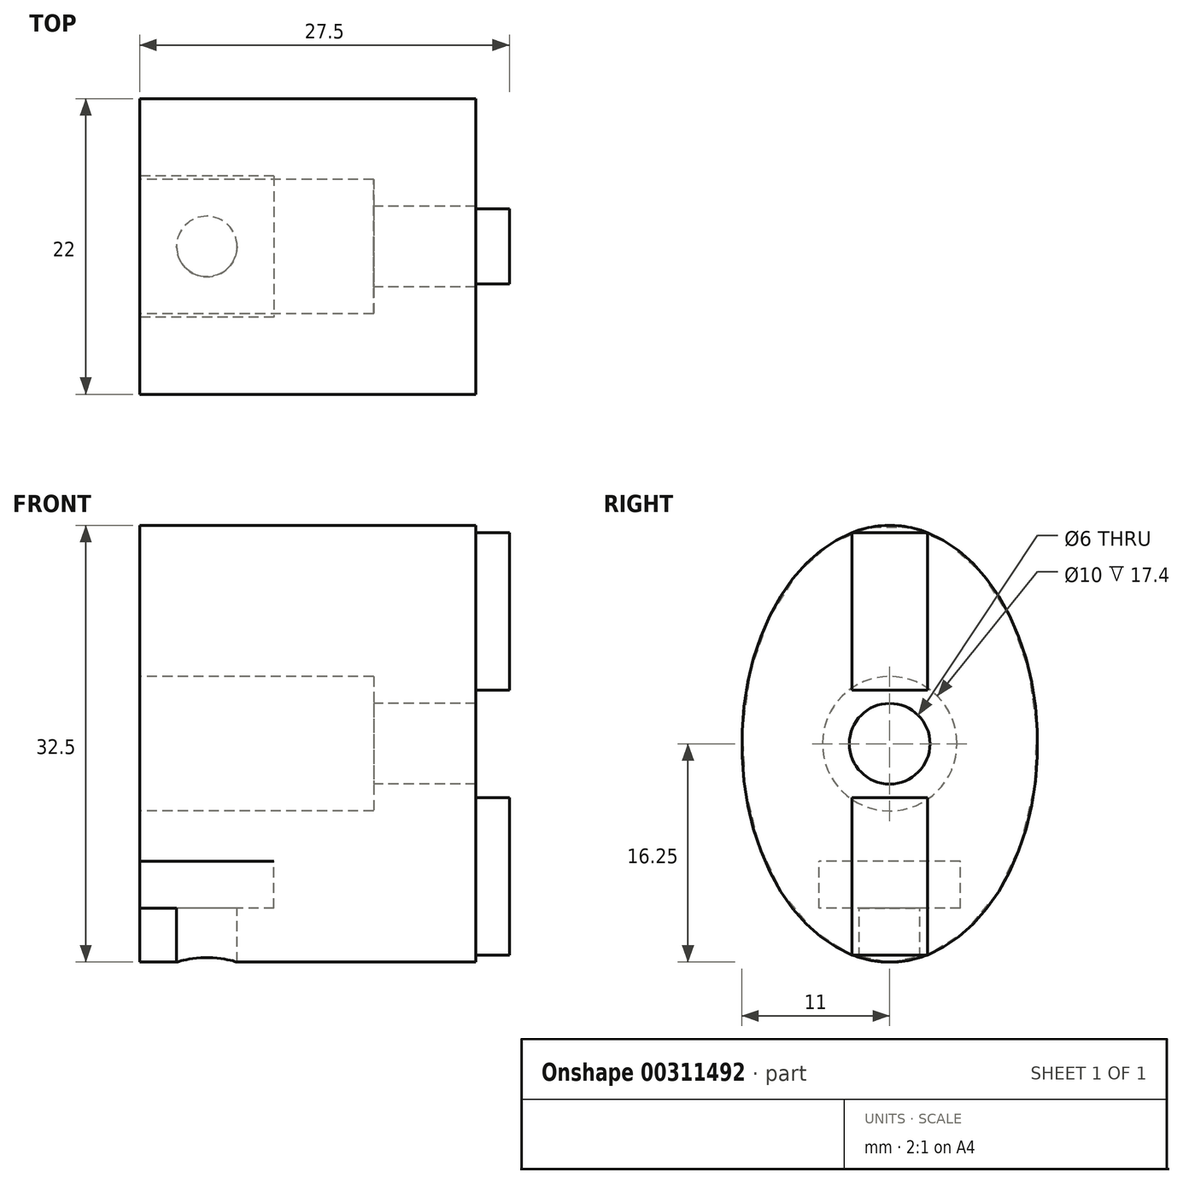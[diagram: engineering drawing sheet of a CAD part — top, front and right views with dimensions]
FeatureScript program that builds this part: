
annotation { "Feature Type Name" : "Feature", "Feature Type Description" : "" }
export const myFeature = defineFeature(function(context is Context, id is Id, definition is map)
    precondition{}
    {
        {
            var Q0;
            Q0=qCreatedBy(makeId("Right.planeOp"),FACE);
            var sketch = newSketch(context, id + "F0", { "sketchPlane" : qUnion([Q0])});
            skEllipse(sketch, "E0", {"center": v(0, 0) * mm, "majorRadius": 16.25 * mm, "minorRadius": 11 * mm, "majorAxis": v(0, -1)});
            skSolve(sketch);
        }
        {
            var Q0;
            Q0=makeQuery(id+"F0.imprint","IMPRINT",FACE,{"disambiguationData":[TD([[makeQuery(id+"F0.imprint","IMPRINT",EDGE,{"derivedFrom":sQuery(id+"F0.wireOp",EDGE,"E0")}),1.0]])]});
            var Q1;
            Q1 = qConstructionFilter(qBodyType(qCreatedBy(id + "F0" ,EDGE), BodyType.WIRE), ConstructionObject.NO);
            extrude(context, id + "F1", {"entities" : qUnion([Q0]), "surfaceEntities" : qUnion([Q1]), "depth" : 25 * mm});
        }
        {
            var Q0;
            Q0=sQuery(id+"F0.wireOp",VERTEX,"E0.center");
            var Q1;
            Q1=makeQuery(id+"F1.opExtrude","SWEPT_BODY",BODY,{"disambiguationData":[OSD([sQuery(id+"F0.wireOp",EDGE,"E0")])]});
            hole(context, id + "F2", {"style" : HoleStyle.C_BORE, "endStyle" : HoleEndStyle.THROUGH, "oppositeDirection" : true, "holeDiameter" : 6 * mm, "cBoreDiameter" : 10 * mm, "cBoreDepth" : 17.4 * mm, "isTappedThrough" : true, "tappedDepth" : 12 * mm, "tapClearance" : 3, "locations" : qUnion([Q0]), "scope" : qUnion([Q1])});
        }
        {
            var Q0;
            Q0=makeQuery(id+"F0.imprint","IMPRINT",FACE,{"disambiguationData":[TD([[makeQuery(id+"F0.imprint","IMPRINT",EDGE,{"derivedFrom":sQuery(id+"F0.wireOp",EDGE,"E0")}),1.0]])]});
            cPlane(context, id + "F3", {"entities" : qUnion([Q0]), "cplaneType" : CPlaneType.OFFSET, "offset" : 0 * mm, "width" : 150 * mm, "height" : 150 * mm});
        }
        {
            var Q0;
            Q0=qCreatedBy(id+"F3.planeOp",FACE);
            var sketch = newSketch(context, id + "F4", { "sketchPlane" : qUnion([Q0])});
            skLineSegment(sketch, "E1.bottom", {"start": v(5.25, -12.25) * mm, "end": v(-5.25, -12.25) * mm});
            skLineSegment(sketch, "E1.top", {"start": v(5.25, -8.75) * mm, "end": v(-5.25, -8.75) * mm});
            skLineSegment(sketch, "E1.left", {"start": v(5.25, -12.25) * mm, "end": v(5.25, -8.75) * mm});
            skLineSegment(sketch, "E1.right", {"start": v(-5.25, -12.25) * mm, "end": v(-5.25, -8.75) * mm});
            skLineSegment(sketch, "E2", {"start": v(0, 0) * mm, "end": v(0, -16.25) * mm, "construction": true});
            skPoint(sketch, "E3", {"position": v(0, -12.25) * mm});
            skSolve(sketch);
        }
        {
            var Q0;
            Q0=makeQuery(id+"F4.imprint","IMPRINT",FACE,{"disambiguationData":[TD([[makeQuery(id+"F4.imprint","IMPRINT",EDGE,{"derivedFrom":sQuery(id+"F4.wireOp",EDGE,"E1.bottom")}),-1.0]])]});
            extrude(context, id + "F5", {"entities" : qUnion([Q0]), "operationType" : NewBodyOperationType.REMOVE, "depth" : 10 * mm});
        }
        {
            var Q0;
            Q0=makeQuery(id+"F5.boolean.opBoolean","COPY",VERTEX,{"derivedFrom":makeQuery(id+"F5.opExtrude","CAP_VERTEX",VERTEX,{"disambiguationData":[OSD([sQuery(id+"F4.wireOp",EDGE,"E1.bottom"),sQuery(id+"F4.wireOp",EDGE,"E1.left")])],"isStart":true})});
            var Q1;
            Q1=makeQuery(id+"F5.boolean.opBoolean","COPY",VERTEX,{"derivedFrom":makeQuery(id+"F5.opExtrude","CAP_VERTEX",VERTEX,{"disambiguationData":[OSD([sQuery(id+"F4.wireOp",EDGE,"E1.bottom"),sQuery(id+"F4.wireOp",EDGE,"E1.right")])],"isStart":true})});
            var Q2;
            Q2=makeQuery(id+"F5.boolean.opBoolean","COPY",VERTEX,{"derivedFrom":makeQuery(id+"F5.opExtrude","CAP_VERTEX",VERTEX,{"disambiguationData":[OSD([sQuery(id+"F4.wireOp",EDGE,"E1.bottom"),sQuery(id+"F4.wireOp",EDGE,"E1.left")])],"isStart":false})});
            cPlane(context, id + "F6", {"entities" : qUnion([Q0, Q1, Q2]), "cplaneType" : CPlaneType.THREE_POINT, "offset" : 25 * mm, "width" : 150 * mm, "height" : 150 * mm});
        }
        {
            var Q0;
            Q0=qCreatedBy(id+"F6.planeOp",FACE);
            var sketch = newSketch(context, id + "F7", { "sketchPlane" : qUnion([Q0])});
            skPoint(sketch, "E4", {"position": v(5, 0) * mm});
            skPoint(sketch, "E5", {"position": v(0, 0) * mm});
            skPoint(sketch, "E6", {"position": v(4.98, -0.01) * mm});
            skSolve(sketch);
        }
        {
            var Q0;
            Q0=sQuery(id+"F7.wireOp",VERTEX,"E4");
            var Q1;
            Q1=makeQuery(id+"F1.opExtrude","SWEPT_BODY",BODY,{"disambiguationData":[OSD([sQuery(id+"F0.wireOp",EDGE,"E0")])]});
            hole(context, id + "F8", {"style" : HoleStyle.SIMPLE, "endStyle" : HoleEndStyle.BLIND, "oppositeDirection" : true, "holeDiameter" : 4.5 * mm, "holeDepth" : 12 * mm, "isTappedThrough" : true, "tappedDepth" : 12 * mm, "tapClearance" : 3, "locations" : qUnion([Q0]), "scope" : qUnion([Q1])});
        }
        {
            var Q0;
            Q0=makeQuery(id+"F1.opExtrude","CAP_FACE",FACE,{"disambiguationData":[OSD([sQuery(id+"F0.wireOp",EDGE,"E0")])],"isStart":false});
            var sketch = newSketch(context, id + "F9", { "sketchPlane" : qUnion([Q0])});
            skLineSegment(sketch, "E7.bottom", {"start": v(-2.8, 15.71) * mm, "end": v(2.8, 15.71) * mm});
            skLineSegment(sketch, "E7.top", {"start": v(-2.8, 4) * mm, "end": v(2.8, 4) * mm});
            skLineSegment(sketch, "E7.left", {"start": v(-2.8, 15.71) * mm, "end": v(-2.8, 4) * mm});
            skLineSegment(sketch, "E7.right", {"start": v(2.8, 15.71) * mm, "end": v(2.8, 4) * mm});
            skLineSegment(sketch, "E8.bottom", {"start": v(-2.8, -4) * mm, "end": v(2.8, -4) * mm});
            skLineSegment(sketch, "E8.top", {"start": v(-2.8, -15.71) * mm, "end": v(2.8, -15.71) * mm});
            skLineSegment(sketch, "E8.left", {"start": v(-2.8, -4) * mm, "end": v(-2.8, -15.71) * mm});
            skLineSegment(sketch, "E8.right", {"start": v(2.8, -4) * mm, "end": v(2.8, -15.71) * mm});
            skPoint(sketch, "E9", {"position": v(0, 4) * mm});
            skSolve(sketch);
        }
        {
            var Q0;
            Q0=makeQuery(id+"F9.imprint","IMPRINT",FACE,{"disambiguationData":[TD([[makeQuery(id+"F9.imprint","IMPRINT",EDGE,{"derivedFrom":sQuery(id+"F9.wireOp",EDGE,"E7.bottom")}),-1.0]])]});
            var Q1;
            Q1=makeQuery(id+"F9.imprint","IMPRINT",FACE,{"disambiguationData":[TD([[makeQuery(id+"F9.imprint","IMPRINT",EDGE,{"derivedFrom":sQuery(id+"F9.wireOp",EDGE,"E8.bottom")}),-1.0]])]});
            extrude(context, id + "F10", {"entities" : qUnion([Q0, Q1]), "operationType" : NewBodyOperationType.ADD, "offsetDistance" : 25 * mm, "depth" : 2.5 * mm});
        }
    });
